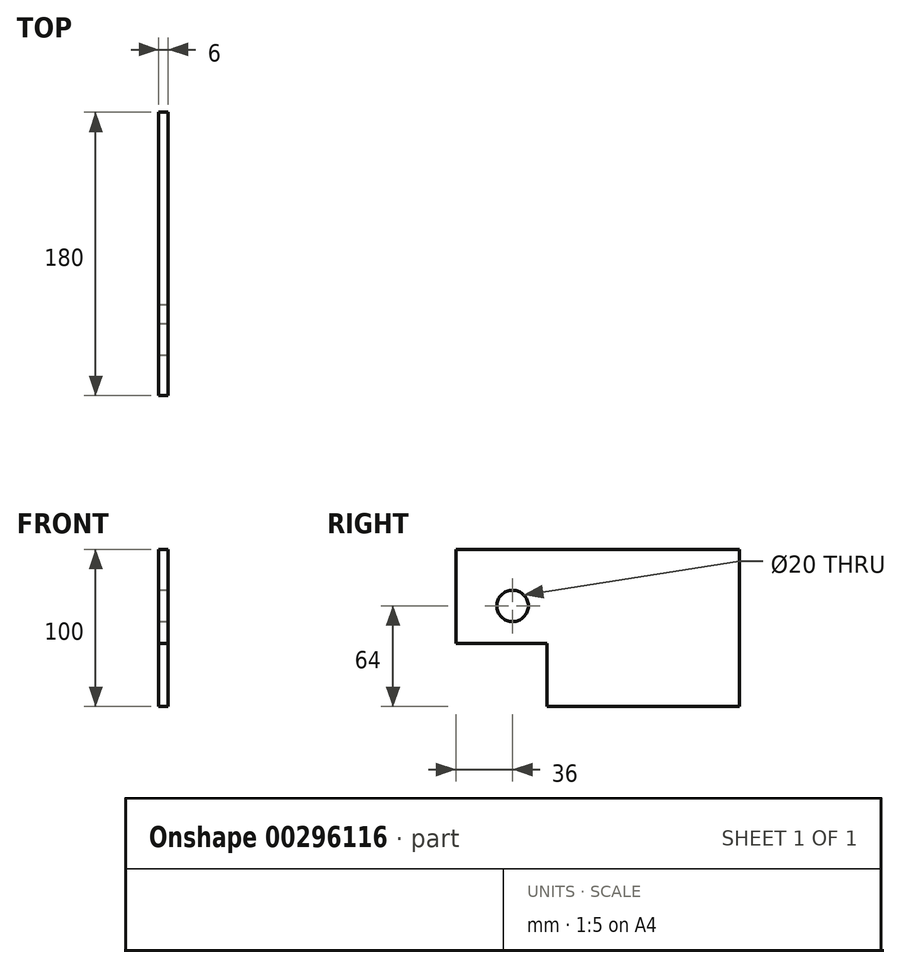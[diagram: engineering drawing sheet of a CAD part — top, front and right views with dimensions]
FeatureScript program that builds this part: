
annotation { "Feature Type Name" : "Feature", "Feature Type Description" : "" }
export const myFeature = defineFeature(function(context is Context, id is Id, definition is map)
    precondition{}
    {
        {
            var Q0;
            Q0=qCreatedBy(makeId("Front.planeOp"),FACE);
            var sketch = newSketch(context, id + "F0", { "sketchPlane" : qUnion([Q0])});
            skLineSegment(sketch, "E0.bottom", {"start": v(3, 50) * mm, "end": v(-3, 50) * mm});
            skLineSegment(sketch, "E0.top", {"start": v(3, -50) * mm, "end": v(-3, -50) * mm});
            skLineSegment(sketch, "E0.left", {"start": v(3, 50) * mm, "end": v(3, -50) * mm});
            skLineSegment(sketch, "E0.right", {"start": v(-3, 50) * mm, "end": v(-3, -50) * mm});
            skPoint(sketch, "E0.middle", {"position": v(0, 0) * mm});
            skSolve(sketch);
        }
        {
            var Q0;
            Q0=makeQuery(id+"F0.imprint","IMPRINT",FACE,{"disambiguationData":[TD([[makeQuery(id+"F0.imprint","IMPRINT",EDGE,{"derivedFrom":sQuery(id+"F0.wireOp",EDGE,"E0.bottom")}),1.0]])]});
            extrude(context, id + "F1", {"entities" : qUnion([Q0]), "oppositeDirection" : true, "depth" : (100 + 80) * mm});
        }
        {
            var Q0;
            Q0=makeQuery(id+"F1.opExtrude","SWEPT_FACE",FACE,{"disambiguationData":[OSD([sQuery(id+"F0.wireOp",EDGE,"E0.left")])]});
            var sketch = newSketch(context, id + "F2", { "sketchPlane" : qUnion([Q0])});
            skCircle(sketch, "E1", {"center": v(36, 14) * mm, "radius": 10 * mm});
            skLineSegment(sketch, "E2.bottom", {"start": v(0, -10) * mm, "end": v(58, -10) * mm});
            skLineSegment(sketch, "E2.top", {"start": v(0, -50) * mm, "end": v(58, -50) * mm});
            skLineSegment(sketch, "E2.left", {"start": v(0, -10) * mm, "end": v(0, -50) * mm});
            skLineSegment(sketch, "E2.right", {"start": v(58, -10) * mm, "end": v(58, -50) * mm});
            skSolve(sketch);
        }
        {
            var Q0;
            Q0=makeQuery(id+"F2.imprint","IMPRINT",FACE,{"disambiguationData":[TD([[makeQuery(id+"F2.imprint","IMPRINT",EDGE,{"derivedFrom":sQuery(id+"F2.wireOp",EDGE,"E1")}),1.0]])]});
            var Q1;
            Q1=makeQuery(id+"F2.imprint","IMPRINT",FACE,{"disambiguationData":[TD([[makeQuery(id+"F2.imprint","IMPRINT",EDGE,{"derivedFrom":sQuery(id+"F2.wireOp",EDGE,"E2.bottom")}),-1.0]])]});
            extrude(context, id + "F3", {"entities" : qUnion([Q0, Q1]), "operationType" : NewBodyOperationType.REMOVE, "endBound" : BoundingType.THROUGH_ALL, "oppositeDirection" : true, "depth" : 25 * mm});
        }
    });
